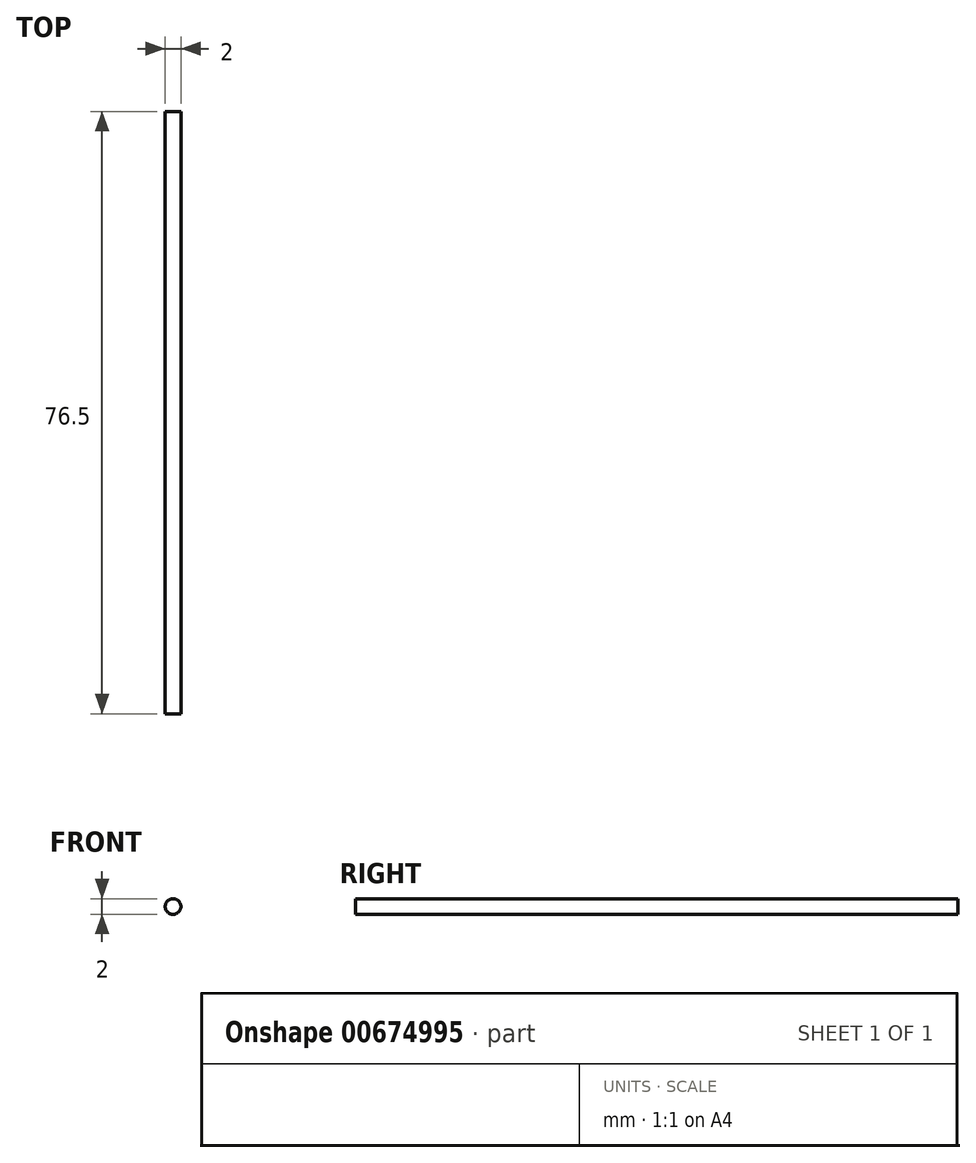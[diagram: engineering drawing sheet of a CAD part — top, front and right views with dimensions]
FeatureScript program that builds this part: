
annotation { "Feature Type Name" : "Feature", "Feature Type Description" : "" }
export const myFeature = defineFeature(function(context is Context, id is Id, definition is map)
    precondition{}
    {
        {
            assignVariable(context, id + "F0", {"name" : "Faktor", "anyValue" : 1.5});
        }
        {
            var Q0;
            Q0=qCreatedBy(makeId("Front.planeOp"),FACE);
            var sketch = newSketch(context, id + "F1", { "sketchPlane" : qUnion([Q0])});
            skCircle(sketch, "E0", {"center": v(0, 0) * mm, "radius": 1 * mm});
            skSolve(sketch);
        }
        {
            var Q0;
            Q0=qSketchRegion(id+"F1",true);
            extrude(context, id + "F2", {"entities" : qUnion([Q0]), "depth" : getVariable(context, 'Faktor') * 51 * mm, "offsetDistance" : 25 * mm});
        }
    });
